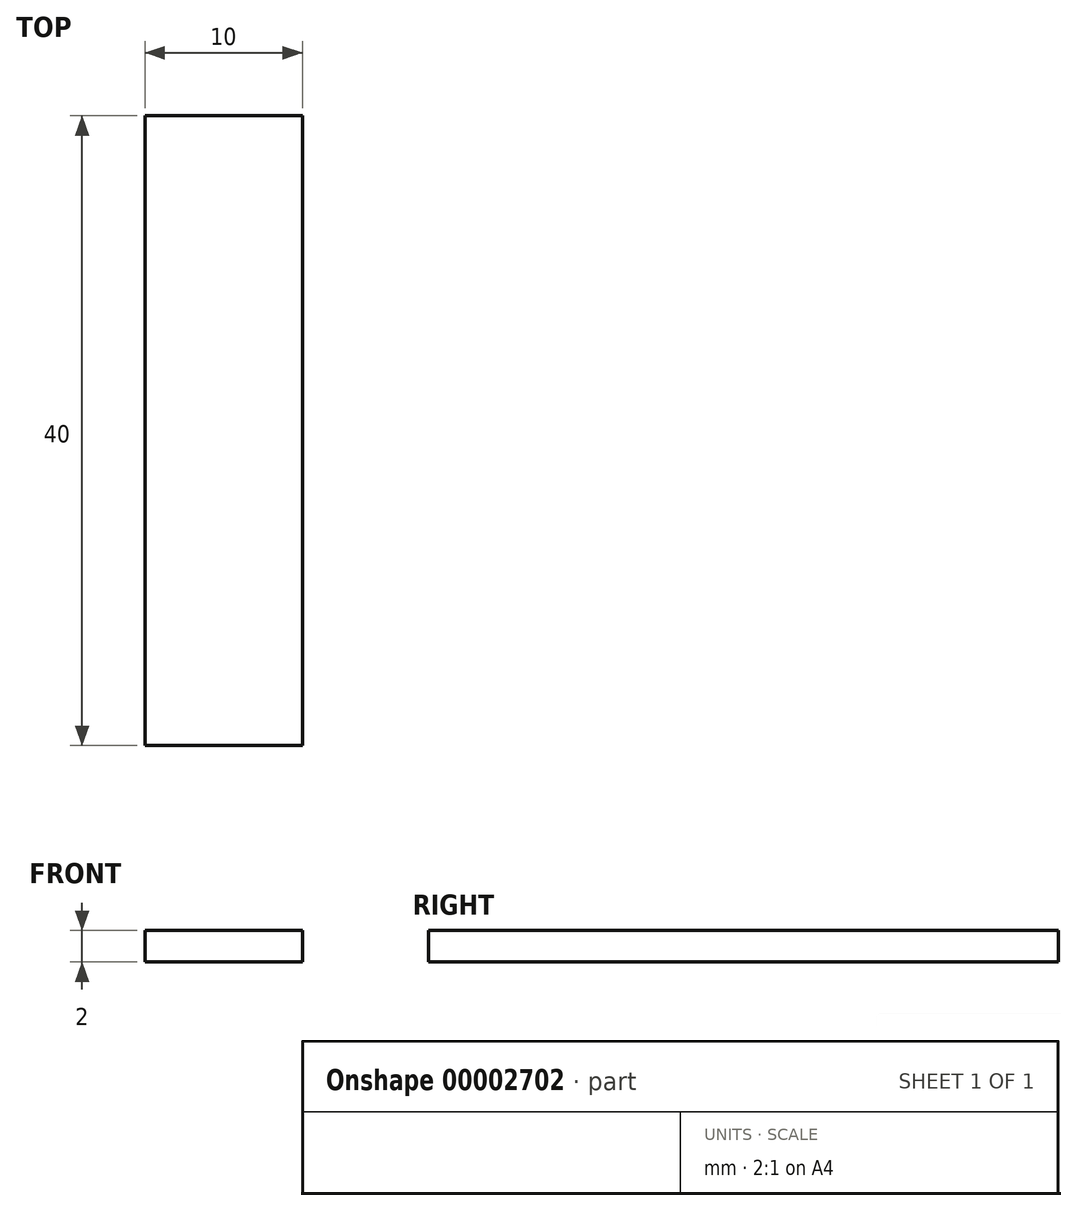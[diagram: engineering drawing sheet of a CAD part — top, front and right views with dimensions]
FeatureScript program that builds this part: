
annotation { "Feature Type Name" : "Feature", "Feature Type Description" : "" }
export const myFeature = defineFeature(function(context is Context, id is Id, definition is map)
    precondition{}
    {
        {
            var Q0;
            Q0=qCreatedBy(makeId("Top.planeOp"),FACE);
            var sketch = newSketch(context, id + "F0", { "sketchPlane" : qUnion([Q0])});
            skLineSegment(sketch, "E0.bottom", {"start": v(0, 0) * mm, "end": v(10, 0) * mm});
            skLineSegment(sketch, "E0.top", {"start": v(0, 40) * mm, "end": v(10, 40) * mm});
            skLineSegment(sketch, "E0.left", {"start": v(0, 0) * mm, "end": v(0, 40) * mm});
            skLineSegment(sketch, "E0.right", {"start": v(10, 0) * mm, "end": v(10, 40) * mm});
            skSolve(sketch);
        }
        {
            var Q0;
            Q0 = qSketchRegion(id + "F0", true);
            extrude(context, id + "F1", {"entities" : qUnion([Q0]), "depth" : 2 * mm});
        }
    });
